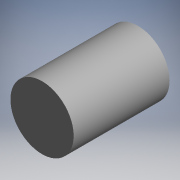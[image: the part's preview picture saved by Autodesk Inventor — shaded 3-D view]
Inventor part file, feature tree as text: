
AUTODESK INVENTOR PART (.ipt)
format: ipt  version: 2019.4 (Build 234330000, 330)  size: 96,256 bytes
history: native  units: mm
features: extrude x2, sketch x2
ambient origin geometry x8: Origin, YZ Plane, XZ Plane, XY Plane, X Axis, Y Axis, Z Axis, Center Point
bodies: Solid1 (feature_tree)
feature tree (4):
  extrude  "Extrusion1"  Depth=34.0mm TaperAngle=0.0deg
  extrude  "Extrusion2"  Depth=8.5mm TaperAngle=0.0deg
  sketch  "Sketch1"  dims[d0=24.4mm d1=34.0mm d2=0.0mm]
  sketch  "Sketch2"  dims[d3=5.0mm d4=8.5mm d5=0.0mm]
